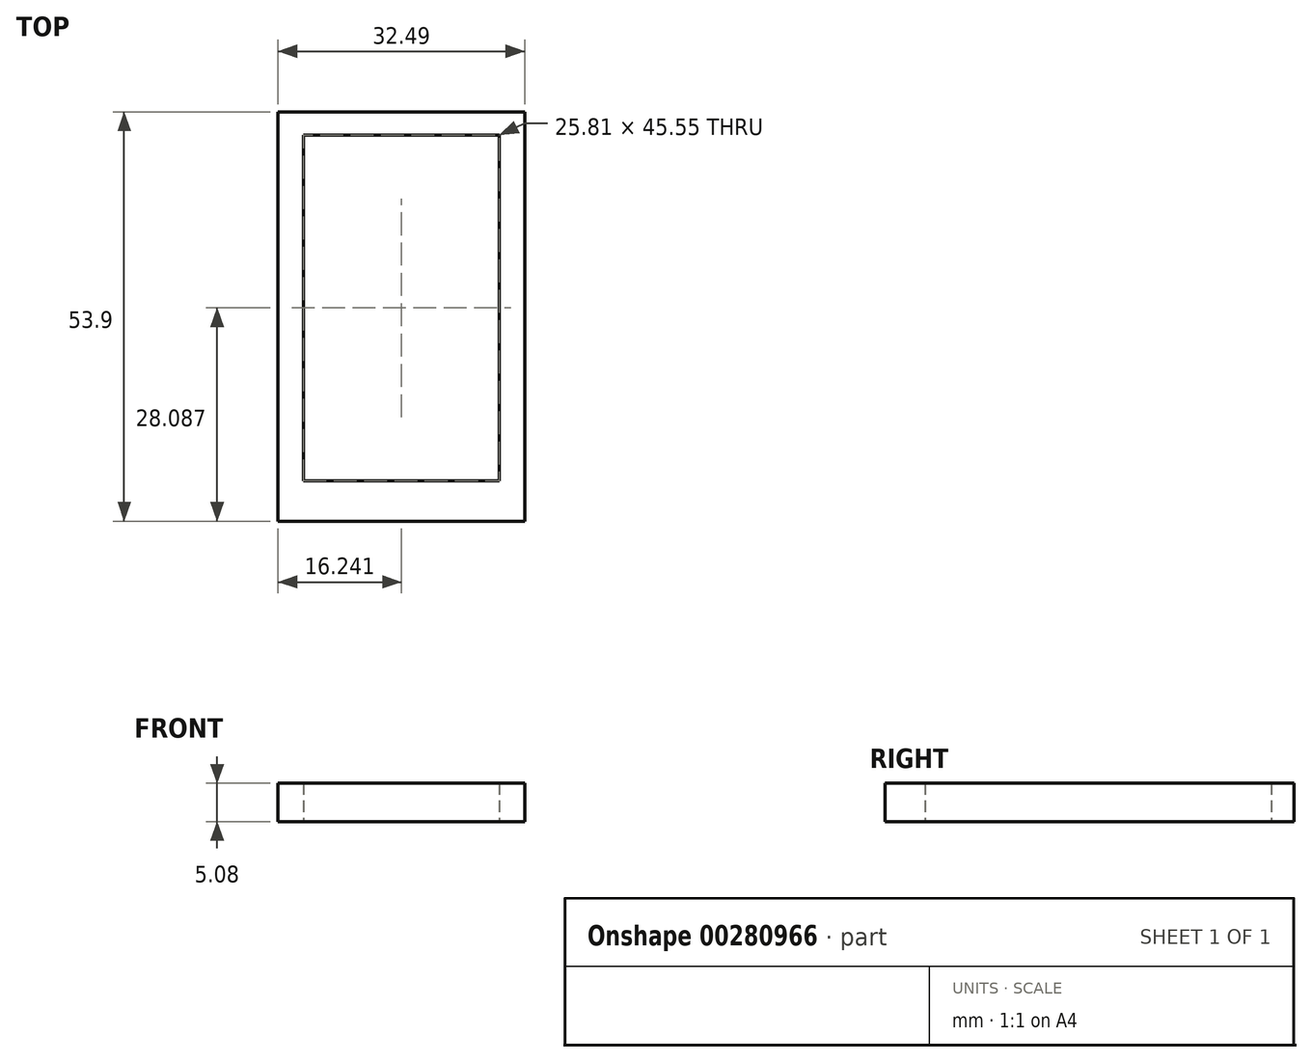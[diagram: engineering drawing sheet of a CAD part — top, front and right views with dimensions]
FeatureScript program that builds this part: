
annotation { "Feature Type Name" : "Feature", "Feature Type Description" : "" }
export const myFeature = defineFeature(function(context is Context, id is Id, definition is map)
    precondition{}
    {
        {
            var Q0;
            Q0=qCreatedBy(makeId("Top.planeOp"),FACE);
            var sketch = newSketch(context, id + "F0", { "sketchPlane" : qUnion([Q0])});
            skLineSegment(sketch, "E0.bottom", {"start": v(-69.53, 53.9) * mm, "end": v(-37.04, 53.9) * mm});
            skLineSegment(sketch, "E0.top", {"start": v(-69.53, 0) * mm, "end": v(-37.04, 0) * mm});
            skLineSegment(sketch, "E0.left", {"start": v(-69.53, 53.9) * mm, "end": v(-69.53, 0) * mm});
            skLineSegment(sketch, "E0.right", {"start": v(-37.04, 53.9) * mm, "end": v(-37.04, 0) * mm});
            skLineSegment(sketch, "E1.bottom", {"start": v(-66.2, 50.86) * mm, "end": v(-40.38, 50.86) * mm});
            skLineSegment(sketch, "E1.top", {"start": v(-66.2, 5.31) * mm, "end": v(-40.38, 5.31) * mm});
            skLineSegment(sketch, "E1.left", {"start": v(-66.2, 50.86) * mm, "end": v(-66.2, 5.31) * mm});
            skLineSegment(sketch, "E1.right", {"start": v(-40.38, 50.86) * mm, "end": v(-40.38, 5.31) * mm});
            skSolve(sketch);
        }
        {
            var Q0;
            Q0=makeQuery(id+"F0.imprint","IMPRINT",FACE,{"disambiguationData":[TD([[makeQuery(id+"F0.imprint","IMPRINT",EDGE,{"derivedFrom":sQuery(id+"F0.wireOp",EDGE,"E0.bottom")}),-1.0]])]});
            extrude(context, id + "F1", {"entities" : qUnion([Q0]), "depth" : 5.08 * mm});
        }
    });
